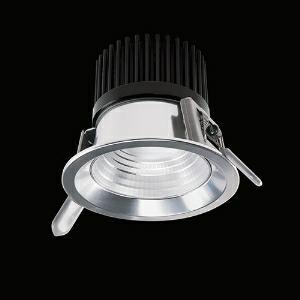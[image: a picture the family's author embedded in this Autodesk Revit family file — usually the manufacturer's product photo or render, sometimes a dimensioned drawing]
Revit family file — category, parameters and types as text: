
# Revit family: spectral_myral_myral_4500-840-s
name_source: partatom
category: Lighting Fixtures
revit_build: Autodesk Revit 2016 (Build: 20150220_1215(x64)
units: mm (PartAtom-declared; Revit-internal decimal feet)

## family parameters
Cut with Voids When Loaded = No
Host = Face
Light Source = No
Part Type = Normal
Room Calculation Point = No
Round Connector Dimension = Use Diameter
Shared = No

## types (1)
- SPECTRAL MYRAL (1 x )
    Apparent Load = 0 VA
    Approval mark = CE
    CIE Flux Codes = 85 100 100 100 100
    Control Gear = Electronic transformer
    Default Elevation = 1800 mm
    Description = SPG0320177
MYRAL recessed spot

Design:
    Height = 0 mm  [stored 0 ft]
    Lamp = 1 x
    Lamp count = 1
    Length = 120 mm
    Luminous efficacy = 0 lm/W
    Manufacturer = Ridi
    ModVariant = No
    Model = MYRAL 4500-840-S
    Mounting Place = Ceiling
    Mounting Type = Recessed
    Number of Poles = 1
    OnlyDefault = Yes
    Power Factor = 1
    Product Name = SPECTRAL MYRAL
    Product group = Downlight recessed
    ProductGroupID = 400
    Protection Class = Protection class
    Protection Degree = IP 20
    RlxData = <blob elided: 38885 chars, md5=8abc0f74>
    Socket = socket
    Standby Power = 0 W
    System Light Flux = 0 lm
    System Power = 0 W
    Type Image = myral_04.jpg
    URL = http://reluxnet.relux.com
    VarID = ---
    Voltage = 0 V
    Weight = 0.00 kg
    Width = 0 mm  [stored 0 ft]

note: [stored X ft] marks values corroborated as IEEE doubles in the binary element streams (Revit-internal decimal feet)

## geometry (parser evidence)
native form markers: Sweep x7
no freeform markers — native parametric forms only
